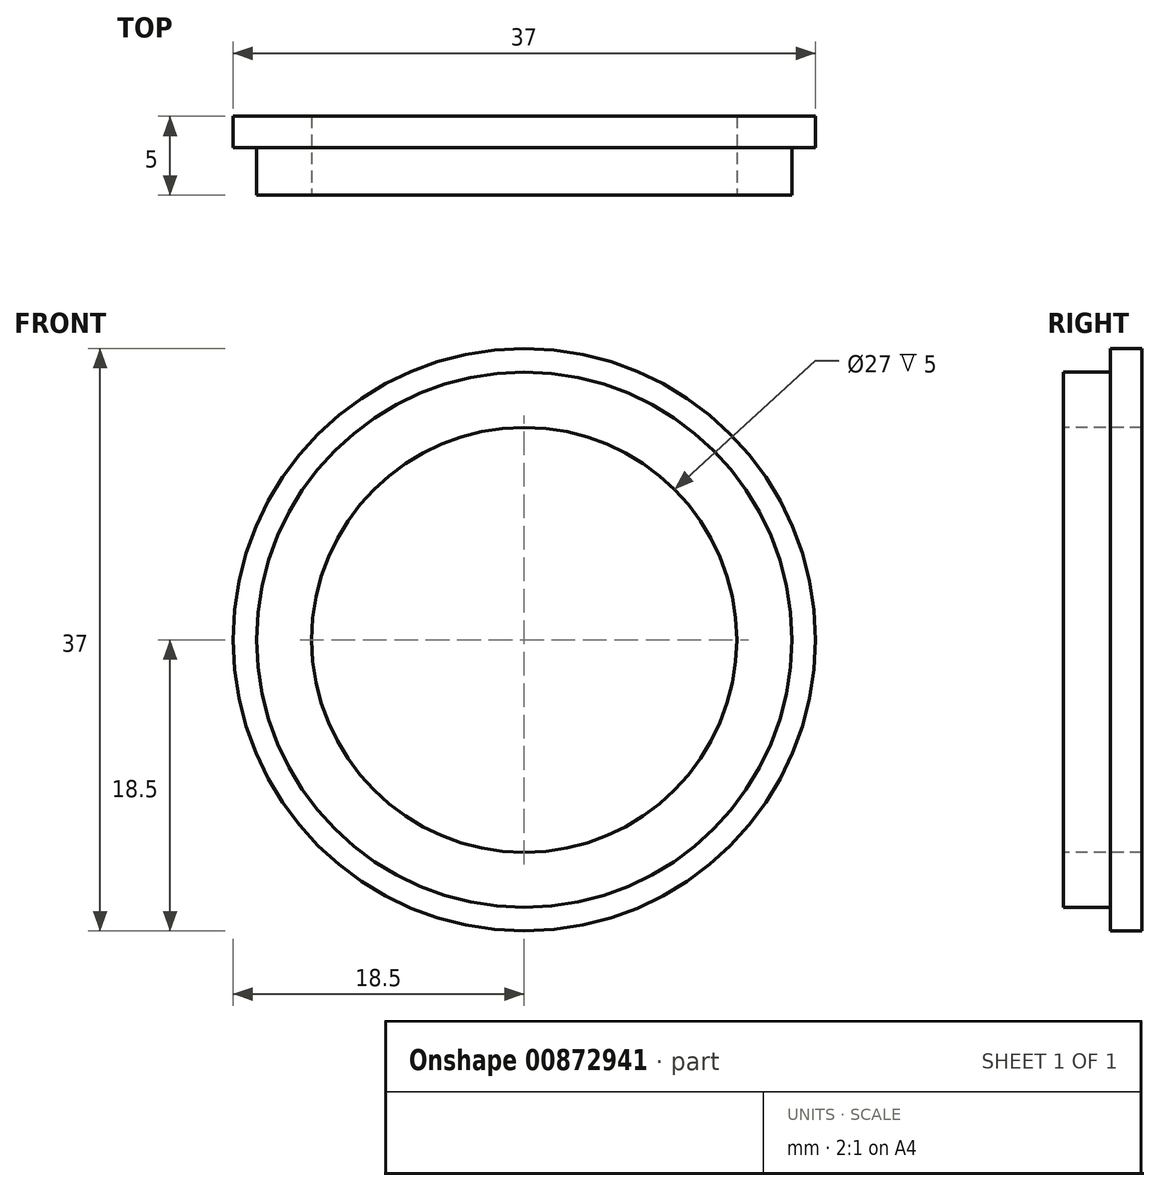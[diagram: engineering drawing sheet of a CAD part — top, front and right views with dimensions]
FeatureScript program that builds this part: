
annotation { "Feature Type Name" : "Feature", "Feature Type Description" : "" }
export const myFeature = defineFeature(function(context is Context, id is Id, definition is map)
    precondition{}
    {
        {
            var Q0;
            Q0=qCreatedBy(makeId("Top.planeOp"),FACE);
            var sketch = newSketch(context, id + "F0", { "sketchPlane" : qUnion([Q0])});
            skLineSegment(sketch, "E0.bottom", {"start": v(13.5, 0) * mm, "end": v(17, 0) * mm, "construction": true});
            skLineSegment(sketch, "E0.top", {"start": v(13.5, -3) * mm, "end": v(17, -3) * mm});
            skLineSegment(sketch, "E0.left", {"start": v(13.5, 0) * mm, "end": v(13.5, -3) * mm});
            skLineSegment(sketch, "E0.right", {"start": v(17, 0) * mm, "end": v(17, -3) * mm});
            skLineSegment(sketch, "E1.top", {"start": v(13.5, 2) * mm, "end": v(18.5, 2) * mm});
            skLineSegment(sketch, "E1.left", {"start": v(13.5, 0) * mm, "end": v(13.5, 2) * mm});
            skLineSegment(sketch, "E1.right", {"start": v(18.5, 0) * mm, "end": v(18.5, 2) * mm});
            skLineSegment(sketch, "E2", {"start": v(0, 0) * mm, "end": v(0, 3.04) * mm});
            skLineSegment(sketch, "E3", {"start": v(17, 0) * mm, "end": v(18.5, 0) * mm});
            skSolve(sketch);
        }
        {
            var Q0;
            Q0=qSketchRegion(id+"F0",true);
            var Q1;
            Q1=sQuery(id+"F0.wireOp",EDGE,"E2");
            revolve(context, id + "F1", {"entities" : qUnion([Q0]), "axis" : qUnion([Q1]), "revolveType" : RevolveType.FULL});
        }
    });
